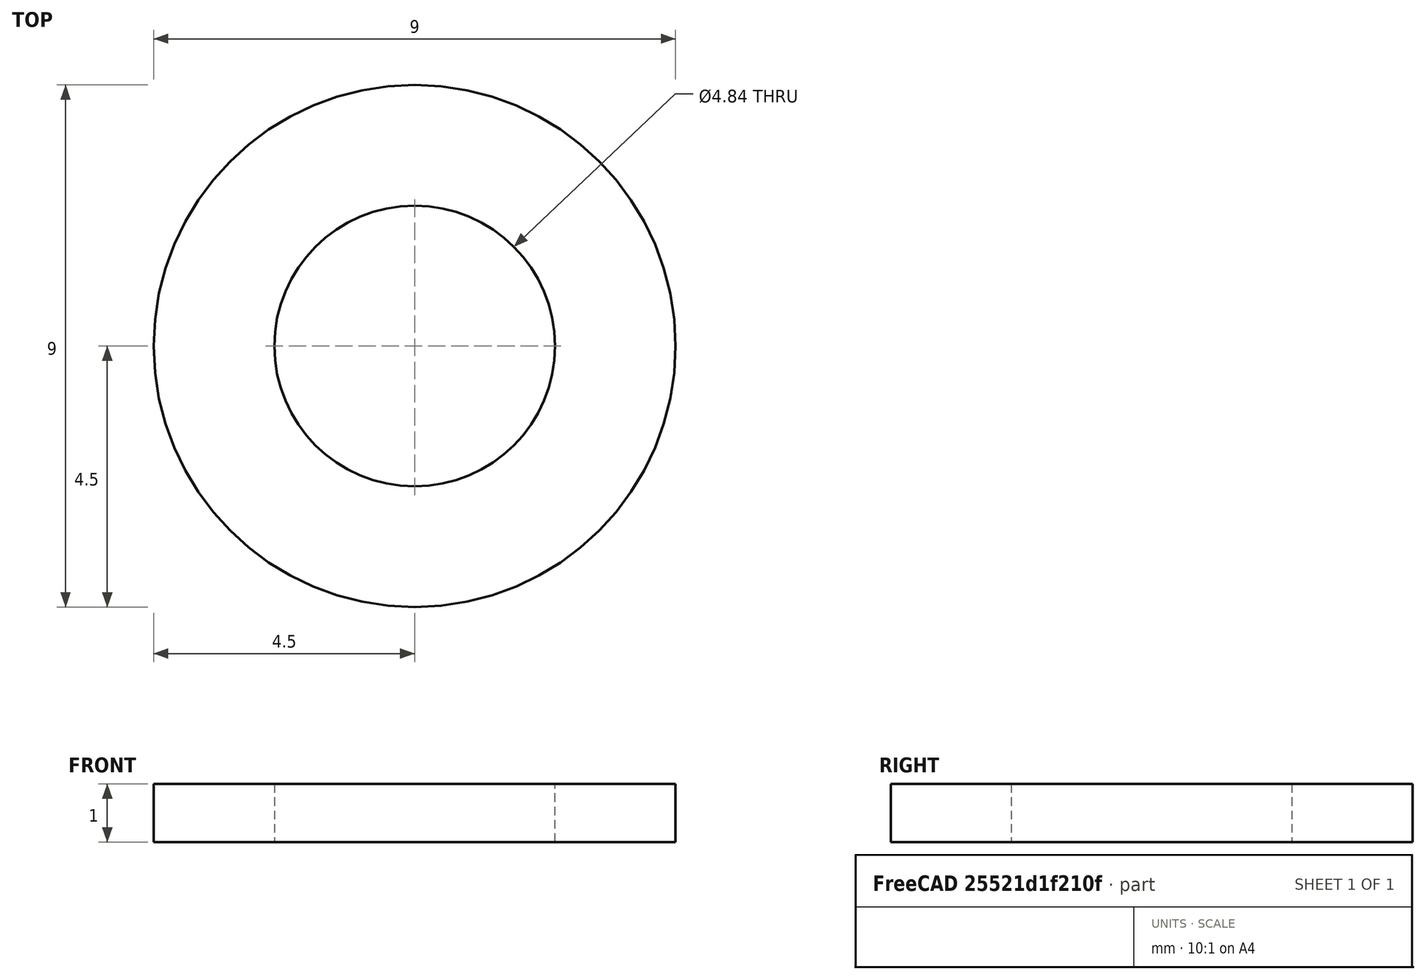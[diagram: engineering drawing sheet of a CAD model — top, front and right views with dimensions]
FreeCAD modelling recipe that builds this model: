
FCSTD DOCUMENT  (FreeCAD 0.18R16146 (Git))
Label: led padder
License: All rights reserved
LicenseURL: http://en.wikipedia.org/wiki/All_rights_reserved
objects: Sketcher::SketchObject×1, PartDesign::Pad×1, PartDesign::Body×1
note: 4 computed .brp shape members not serialized (recipe doc carries the construction recipe); baked Part::Feature solids carry a one-line shape summary decoded from their .brp

FEATURE [Sketcher::SketchObject] Sketch
  MapMode = 5
  Support = -> [XY_Plane]
  sketch-geometry (2):
    g0: Circle CenterX=0 CenterY=0 CenterZ=0 NormalX=0 NormalY=0 NormalZ=1 AngleXU=0 Radius=2.42
    g1: Circle CenterX=0 CenterY=0 CenterZ=0 NormalX=0 NormalY=0 NormalZ=1 AngleXU=0 Radius=4.5
  constraints (4):
    c: Coincident(g0,g-1)
    c: Coincident(g1,g0)
    c: Radius(g0) = 2.42
    c: Radius(g1) = 4.5
FEATURE [PartDesign::Pad] Pad
  Length = 1
  Length2 = 100
  Profile = -> Sketch
  Type = 0
FEATURE [PartDesign::Body] Body
  Group = -> [Sketch,Pad]
  Origin = -> Origin
  Tip = -> Pad
